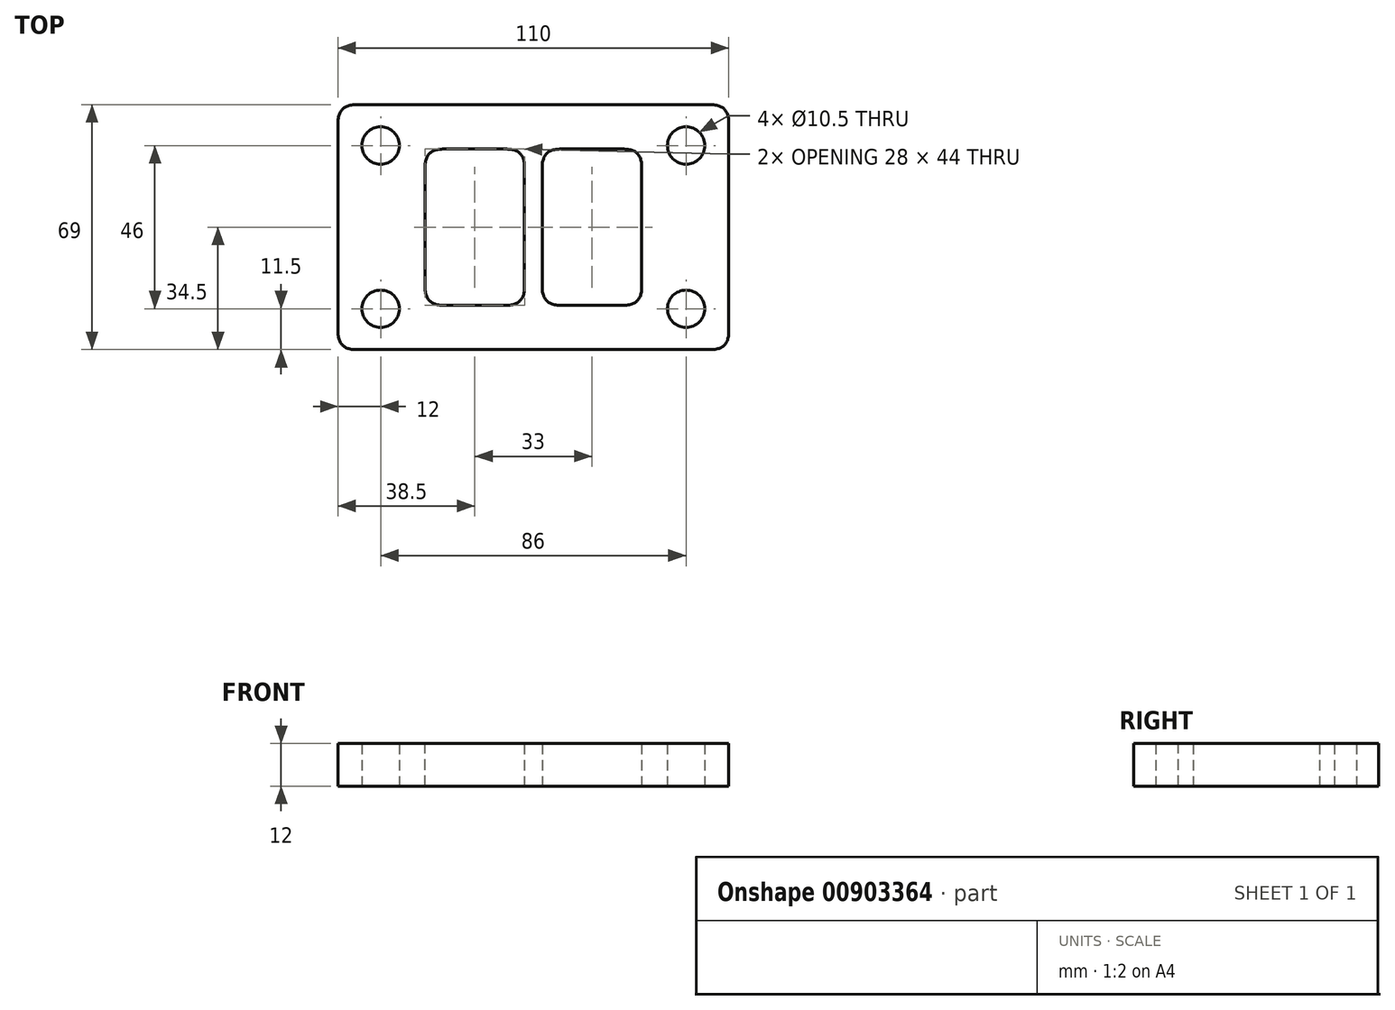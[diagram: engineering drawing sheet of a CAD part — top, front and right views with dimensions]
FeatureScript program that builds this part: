
annotation { "Feature Type Name" : "Feature", "Feature Type Description" : "" }
export const myFeature = defineFeature(function(context is Context, id is Id, definition is map)
    precondition{}
    {
        {
            var Q0;
            Q0=qCreatedBy(makeId("Top.planeOp"),FACE);
            var sketch = newSketch(context, id + "F0", { "sketchPlane" : qUnion([Q0])});
            skLineSegment(sketch, "E0.bottom", {"start": v(-55, 34.5) * mm, "end": v(55, 34.5) * mm});
            skLineSegment(sketch, "E0.top", {"start": v(-55, -34.5) * mm, "end": v(55, -34.5) * mm});
            skLineSegment(sketch, "E0.left", {"start": v(-55, 34.5) * mm, "end": v(-55, -34.5) * mm});
            skLineSegment(sketch, "E0.right", {"start": v(55, 34.5) * mm, "end": v(55, -34.5) * mm});
            skLineSegment(sketch, "E1.bottom", {"start": v(30.5, -22) * mm, "end": v(-30.5, -22) * mm});
            skLineSegment(sketch, "E1.top", {"start": v(30.5, 22) * mm, "end": v(-30.5, 22) * mm});
            skLineSegment(sketch, "E1.left", {"start": v(30.5, -22) * mm, "end": v(30.5, 22) * mm});
            skLineSegment(sketch, "E1.right", {"start": v(-30.5, -22) * mm, "end": v(-30.5, 22) * mm});
            skPoint(sketch, "E1.middle", {"position": v(0, 0) * mm});
            skLineSegment(sketch, "E2", {"start": v(-30.5, 0) * mm, "end": v(-55, 0) * mm, "construction": true});
            skLineSegment(sketch, "E3", {"start": v(-3.33, -22) * mm, "end": v(-3.33, -34.5) * mm, "construction": true});
            skLineSegment(sketch, "E4", {"start": v(-2.5, 22) * mm, "end": v(-2.5, -22) * mm});
            skLineSegment(sketch, "E5", {"start": v(2.5, 22) * mm, "end": v(2.5, -22) * mm});
            skLineSegment(sketch, "E6", {"start": v(-2.5, 13.2) * mm, "end": v(2.5, 13.2) * mm, "construction": true});
            skLineSegment(sketch, "E7", {"start": v(2.5, 7.97) * mm, "end": v(30.5, 7.97) * mm, "construction": true});
            skCircle(sketch, "E8", {"center": v(-43, 23) * mm, "radius": 5.25 * mm});
            skCircle(sketch, "E9", {"center": v(43, 23) * mm, "radius": 5.25 * mm});
            skCircle(sketch, "E10", {"center": v(43, -23) * mm, "radius": 5.25 * mm});
            skCircle(sketch, "E11", {"center": v(-43, -23) * mm, "radius": 5.25 * mm});
            skLineSegment(sketch, "E12", {"start": v(-43, 23) * mm, "end": v(-55, 23) * mm, "construction": true});
            skLineSegment(sketch, "E13", {"start": v(-43, 23) * mm, "end": v(-43, 34.5) * mm, "construction": true});
            skLineSegment(sketch, "E14", {"start": v(43, 23) * mm, "end": v(43, 34.5) * mm, "construction": true});
            skLineSegment(sketch, "E15", {"start": v(43, 23) * mm, "end": v(55, 23) * mm, "construction": true});
            skLineSegment(sketch, "E16", {"start": v(43, -23) * mm, "end": v(55, -23) * mm, "construction": true});
            skLineSegment(sketch, "E17", {"start": v(43, -23) * mm, "end": v(43, -34.5) * mm, "construction": true});
            skLineSegment(sketch, "E18", {"start": v(-43, -23) * mm, "end": v(-43, -34.5) * mm, "construction": true});
            skLineSegment(sketch, "E19", {"start": v(-43, -23) * mm, "end": v(-55, -23) * mm, "construction": true});
            skSolve(sketch);
        }
        {
            var Q0;
            Q0=makeQuery(id+"F0.imprint","IMPRINT",FACE,{"disambiguationData":[TD([[makeQuery(id+"F0.imprint","IMPRINT",EDGE,{"derivedFrom":sQuery(id+"F0.wireOp",EDGE,"E0.bottom")}),-1.0]])]});
            var Q1;
            {var subQ0=sQuery(id+"F0.wireOp",EDGE,"E4");Q1=makeQuery(id+"F0.imprint","IMPRINT",FACE,{"disambiguationData":[TD([[makeQuery(id+"F0.imprint","IMPRINT",EDGE,{"derivedFrom":subQ0}),1.0]])]});}
            extrude(context, id + "F1", {"entities" : qUnion([Q0, Q1]), "depth" : 12 * mm, "offsetDistance" : 25 * mm});
        }
        {
            var Q0;
            Q0=makeQuery(id+"F1.opExtrude","SWEPT_EDGE",EDGE,{"disambiguationData":[OSD([sQuery(id+"F0.wireOp",EDGE,"E1.top"),sQuery(id+"F0.wireOp",EDGE,"E1.right")])]});
            var Q1;
            Q1=makeQuery(id+"F1.opExtrude","SWEPT_EDGE",EDGE,{"disambiguationData":[OSD([sQuery(id+"F0.wireOp",EDGE,"E1.top"),sQuery(id+"F0.wireOp",EDGE,"E5")])]});
            var Q2;
            Q2=makeQuery(id+"F1.opExtrude","SWEPT_EDGE",EDGE,{"disambiguationData":[OSD([sQuery(id+"F0.wireOp",EDGE,"E0.top"),sQuery(id+"F0.wireOp",EDGE,"E0.right")])]});
            var Q3;
            Q3=makeQuery(id+"F1.opExtrude","SWEPT_EDGE",EDGE,{"disambiguationData":[OSD([sQuery(id+"F0.wireOp",EDGE,"E0.bottom"),sQuery(id+"F0.wireOp",EDGE,"E0.right")])]});
            var Q4;
            Q4=makeQuery(id+"F1.opExtrude","SWEPT_EDGE",EDGE,{"disambiguationData":[OSD([sQuery(id+"F0.wireOp",EDGE,"E1.bottom"),sQuery(id+"F0.wireOp",EDGE,"E1.left")])]});
            var Q5;
            Q5=makeQuery(id+"F1.opExtrude","SWEPT_EDGE",EDGE,{"disambiguationData":[OSD([sQuery(id+"F0.wireOp",EDGE,"E1.bottom"),sQuery(id+"F0.wireOp",EDGE,"E4")])]});
            var Q6;
            Q6=makeQuery(id+"F1.opExtrude","SWEPT_EDGE",EDGE,{"disambiguationData":[OSD([sQuery(id+"F0.wireOp",EDGE,"E0.top"),sQuery(id+"F0.wireOp",EDGE,"E0.left")])]});
            var Q7;
            Q7=makeQuery(id+"F1.opExtrude","SWEPT_EDGE",EDGE,{"disambiguationData":[OSD([sQuery(id+"F0.wireOp",EDGE,"E0.bottom"),sQuery(id+"F0.wireOp",EDGE,"E0.left")])]});
            var Q8;
            Q8=makeQuery(id+"F1.opExtrude","SWEPT_EDGE",EDGE,{"disambiguationData":[OSD([sQuery(id+"F0.wireOp",EDGE,"E1.top"),sQuery(id+"F0.wireOp",EDGE,"E1.left")])]});
            var Q9;
            Q9=makeQuery(id+"F1.opExtrude","SWEPT_EDGE",EDGE,{"disambiguationData":[OSD([sQuery(id+"F0.wireOp",EDGE,"E1.top"),sQuery(id+"F0.wireOp",EDGE,"E4")])]});
            var Q10;
            Q10=makeQuery(id+"F1.opExtrude","SWEPT_EDGE",EDGE,{"disambiguationData":[OSD([sQuery(id+"F0.wireOp",EDGE,"E1.bottom"),sQuery(id+"F0.wireOp",EDGE,"E1.right")])]});
            var Q11;
            Q11=makeQuery(id+"F1.opExtrude","SWEPT_EDGE",EDGE,{"disambiguationData":[OSD([sQuery(id+"F0.wireOp",EDGE,"E1.bottom"),sQuery(id+"F0.wireOp",EDGE,"E5")])]});
            fillet(context, id + "F2", {"entities" : qUnion([Q0, Q1, Q2, Q3, Q4, Q5, Q6, Q7, Q8, Q9, Q10, Q11]), "radius" : 5 * mm, "rho" : 0.5, "crossSection" : FilletCrossSection.CONIC, "allowEdgeOverflow" : false});
        }
    });
